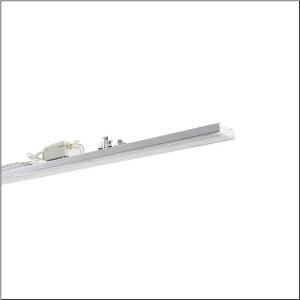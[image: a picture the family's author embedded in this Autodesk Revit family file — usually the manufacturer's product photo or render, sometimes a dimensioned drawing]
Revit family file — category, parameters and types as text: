
# Revit family: licross_r__21_recessed_ho_52te12dv4l2m_40f6
name_source: partatom
category: Lighting Fixtures
units: mm (PartAtom-declared; Revit-internal decimal feet)

## family parameters
Cut with Voids When Loaded = No
Host = Face
Light Source = No
Part Type = Normal
Room Calculation Point = No
Round Connector Dimension = Use Diameter
Shared = No

## types (1)
- --- (1 x LED, 22710 lm, 125.6 W, 4000K)
    Apparent Load = 126 VA
    CIE Flux Codes = 69 91 98 100 100
    Color Rendering = 80
    Color Temperature = 4000K
    Default Elevation = 1800 mm
    Description = Licross® 21 Recessed HO, luminaire insert, of sheet steel, galvanised, coil coated, white, length: 2.250mm, width: 66mm, height: 67mm, LED rated luminous flux: 22.710lm, light colour: 840, control gear: DALI 2, with plug, 5-pole, with phase selection, mains connection: 220..240V, AC, 50/60Hz, rated input power: 126W, halogen-free wiring, primary optical cover: cover, of PMMA, light emission: direct distribution, primary light characteristic: symmetric, protection rating (complete): IP54, insulation class (complete): insulation class I (protective earthing), certification: CE, ENEC, VDE, UKCA, protection symbol: D if used in an environment with non-conductive dust loads with corresponding accessories, impact resistance: IK06, permissible ambient temperature for indoor applications: -40..+30°C, corresponds to IFS (International Featured Standards) requirements for safety and quality in the food industry, reducing of maximum allowable ambient temperature of 5°C with ceiling mounting, LABS conformity tested according to VDMA 24364:2018-05, packaging unit: 1 piece
    Height = 58 mm
    Lamp = 1 x LED
    Lamp Light Flux = 22710 lm
    Lamp Power = 125.6 W
    Lamp count = 1
    Length = 2250 mm
    Luminous efficacy = 181 lm/W
    Manufacturer = Siteco
    ModVariant = No
    Model = 52TE12DV4L2M
    Mounting Place = Ceiling
    Mounting Type = Pendant
    Number of Poles = 1
    OnlyDefault = Yes
    Power Factor = 1
    Product Name = Licross® 21 Recessed HO
    Product group = luminaire insert
    ProductGroupID = 901
    Protection Class = Protection class I
    Protection Degree = IP 54
    RLX_Detail_Level = 1
    RLX_Emergency_Light_Flux = 0 lm
    RLX_Emergency_Type = 0
    RLX_Emergency_Type_DB = No
    RlxData = <blob elided: 29409 chars, md5=8f2ad8df>
    Socket = socket
    Standby Power = 0 W
    System Light Flux = 22710 lm
    System Power = 126 W
    Type Comments = factory setting: luminous flux: 100 % | dim-lin: 254 | 489 mA
    Type Image = l_1296930.jpg
    URL = http://relux.com
    VarID = @adj_046681
    Voltage = 0 V
    Weight = 0.00 kg
    Width = 66 mm

## geometry (parser evidence)
native form markers: Blend x4, Sweep x10
no freeform markers — native parametric forms only
